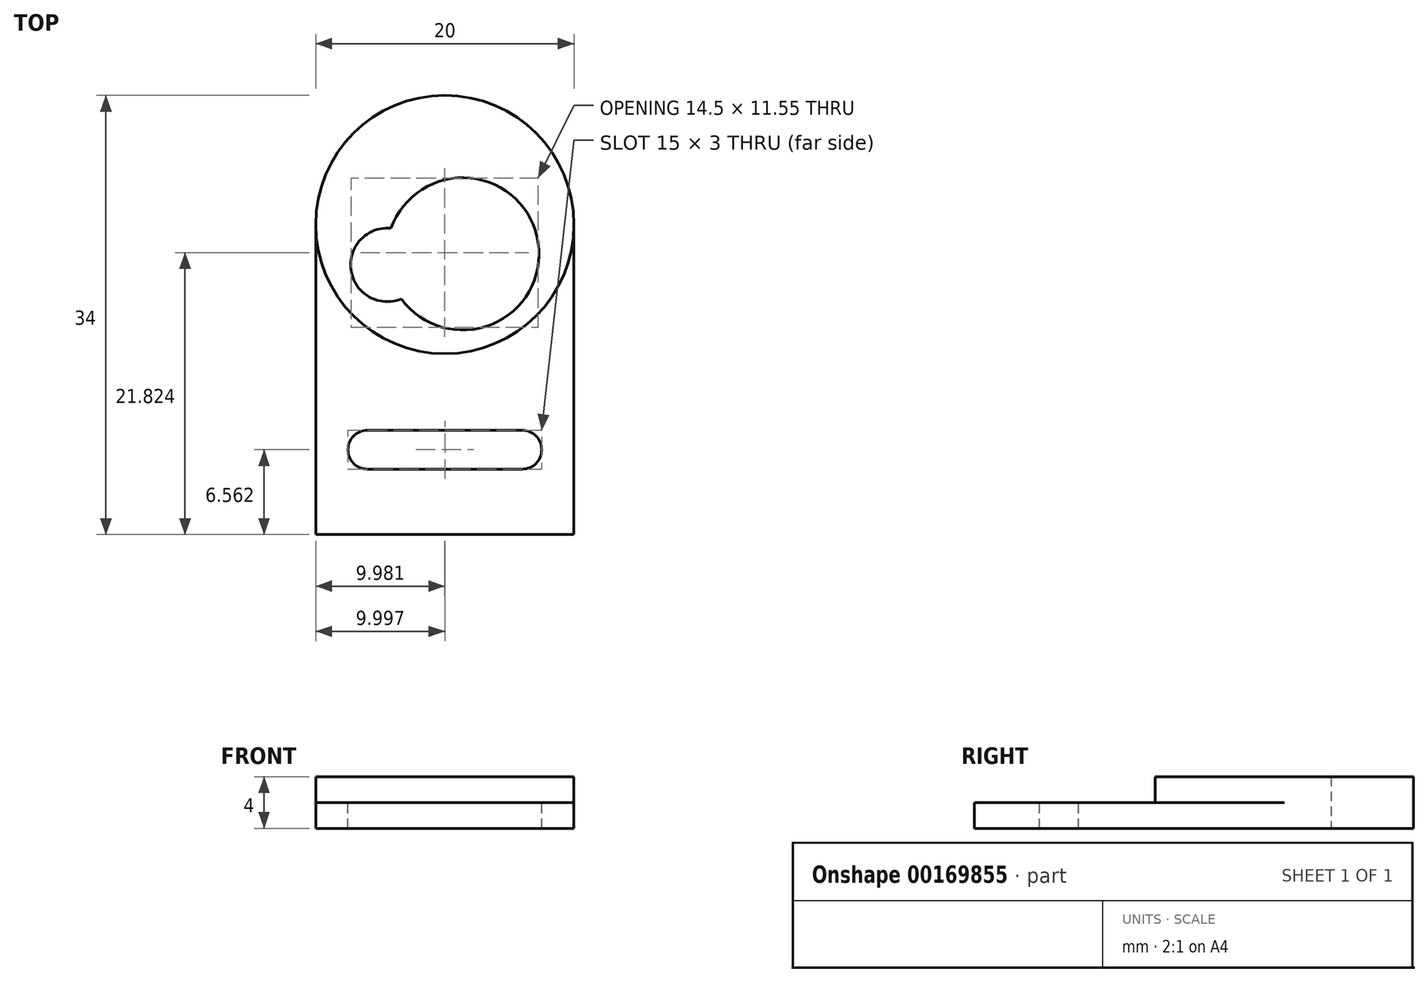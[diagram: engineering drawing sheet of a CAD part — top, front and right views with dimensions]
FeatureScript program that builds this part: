
annotation { "Feature Type Name" : "Feature", "Feature Type Description" : "" }
export const myFeature = defineFeature(function(context is Context, id is Id, definition is map)
    precondition{}
    {
        {
            var Q0;
            Q0=qCreatedBy(makeId("Top.planeOp"),FACE);
            var sketch = newSketch(context, id + "F0", { "sketchPlane" : qUnion([Q0])});
            skCircle(sketch, "E0", {"center": v(-56.96, 27.83) * mm, "radius": 10 * mm});
            skLineSegment(sketch, "E1", {"start": v(-66.96, 27.83) * mm, "end": v(-66.96, 3.83) * mm});
            skLineSegment(sketch, "E2", {"start": v(-66.96, 3.83) * mm, "end": v(-46.96, 3.83) * mm});
            skLineSegment(sketch, "E3", {"start": v(-46.96, 3.83) * mm, "end": v(-46.96, 27.83) * mm});
            skLineSegment(sketch, "E4", {"start": v(-65.63, 11.83) * mm, "end": v(-46.96, 11.83) * mm, "construction": true});
            skLineSegment(sketch, "E5", {"start": v(-66.96, 8.83) * mm, "end": v(-46.96, 8.83) * mm, "construction": true});
            skLineSegment(sketch, "E6", {"start": v(-56.96, 3.83) * mm, "end": v(-56.96, 17.83) * mm, "construction": true});
            skLineSegment(sketch, "E7.bottom", {"start": v(-62.96, 11.9) * mm, "end": v(-50.96, 11.9) * mm});
            skLineSegment(sketch, "E7.top", {"start": v(-62.96, 8.9) * mm, "end": v(-50.96, 8.9) * mm});
            skLineSegment(sketch, "E7.left", {"start": v(-62.96, 8.9) * mm, "end": v(-62.96, 8.83) * mm});
            skLineSegment(sketch, "E7.right", {"start": v(-50.96, 8.9) * mm, "end": v(-50.96, 8.83) * mm});
            skPoint(sketch, "E8", {"position": v(-56.96, 11.9) * mm});
            skArc(sketch, "E9", {"start": v(-50.96, 8.9) * mm, "mid": v(-49.46, 10.4) * mm, "end": v(-50.96, 11.9) * mm});
            skArc(sketch, "E10", {"start": v(-62.96, 11.9) * mm, "mid": v(-64.46, 10.4) * mm, "end": v(-62.96, 8.9) * mm});
            skCircle(sketch, "E11", {"center": v(-55.57, 25.56) * mm, "radius": 5.9 * mm});
            skCircle(sketch, "E12", {"center": v(-61.4, 24.7) * mm, "radius": 2.85 * mm});
            skSolve(sketch);
        }
        {
            var Q0;
            {var subQ0=sQuery(id+"F0.wireOp",EDGE,"E0");var subQ1=makeQuery(id+"F0.imprint","INTERSECT",VERTEX,{"derivedFrom":[subQ0,sQuery(id+"F0.wireOp",EDGE,"E1")]});Q0=makeQuery(id+"F0.imprint","IMPRINT",FACE,{"disambiguationData":[TD([[makeQuery(id+"F0.imprint","IMPRINT",EDGE,{"disambiguationData":[TD([[subQ1,1.0]])],"derivedFrom":subQ0}),1.0]])]});}
            extrude(context, id + "F1", {"entities" : qUnion([Q0]), "depth" : 2 * mm});
        }
        {
            var Q0;
            Q0 = qSketchRegion(id + "F0", true);
            extrude(context, id + "F2", {"entities" : qUnion([Q0]), "operationType" : NewBodyOperationType.ADD, "oppositeDirection" : true, "depth" : 2 * mm});
        }
    });
